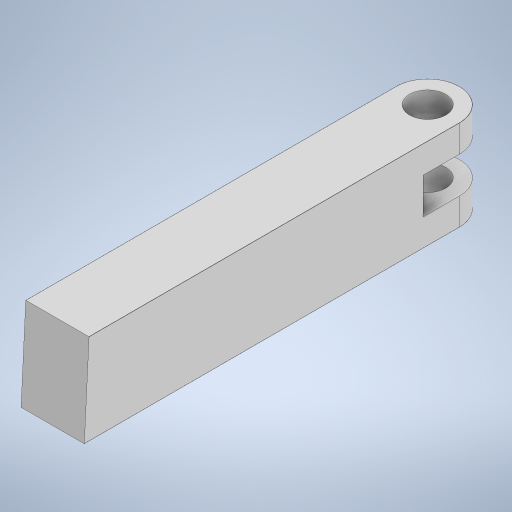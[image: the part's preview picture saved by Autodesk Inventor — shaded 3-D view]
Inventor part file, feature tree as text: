
AUTODESK INVENTOR PART (.ipt)
format: ipt  version: 2023.2 (Build 272271030, 271C)  size: 275,968 bytes
history: native  units: mm
features: chamfer x4, extrude x3, sketch x3, fillet x2, draft x1
ambient origin geometry x8: Origin, YZ Plane, XZ Plane, XY Plane, X Axis, Y Axis, Z Axis, Center Point
bodies: Solid1 (feature_tree)
feature tree (13):
  extrude  "Extrusion1"  Depth=14.0mm
  fillet  "Fillet1"  Radius=14.0mm
  extrude  "Extrusion2"  Depth=8.0mm
  extrude  "Extrusion3"  Depth=6.0mm TaperAngle=0.0deg
  fillet  "Fillet2"  Radius=7.0mm
  draft  "FaceDraft1"
  chamfer  "Chamfer1"  Distance=15.0mm
  chamfer  "Chamfer2"  Distance=8.0mm
  chamfer  "Chamfer3"  Distance=90.0mm
  chamfer  "Chamfer4"  Distance=8.0mm
  sketch  "Sketch1"  dims[d4=45.0mm d5=45.0mm d6=14.0mm]
  sketch  "Sketch2"  dims[d7=90.0mm d8=8.0mm]
  sketch  "Sketch3"  dims[d9=7.0mm d10=6.0mm d11=0.0mm d12=7.0mm d13=15.0mm d14=8.0mm d15=0.0mm d16=90.0mm d17=8.0mm d18=7.0mm d19=6.0mm d20=0.0mm d21=7.0mm d22=0.523599mm d23=0.02mm d24=2.0mm d25=45.0deg d26=0.02mm d27=2.0mm d28=45.0deg d29=0.02mm d30=2.0mm d31=45.0deg d32=0.02mm d33=2.0mm d34=45.0deg]
